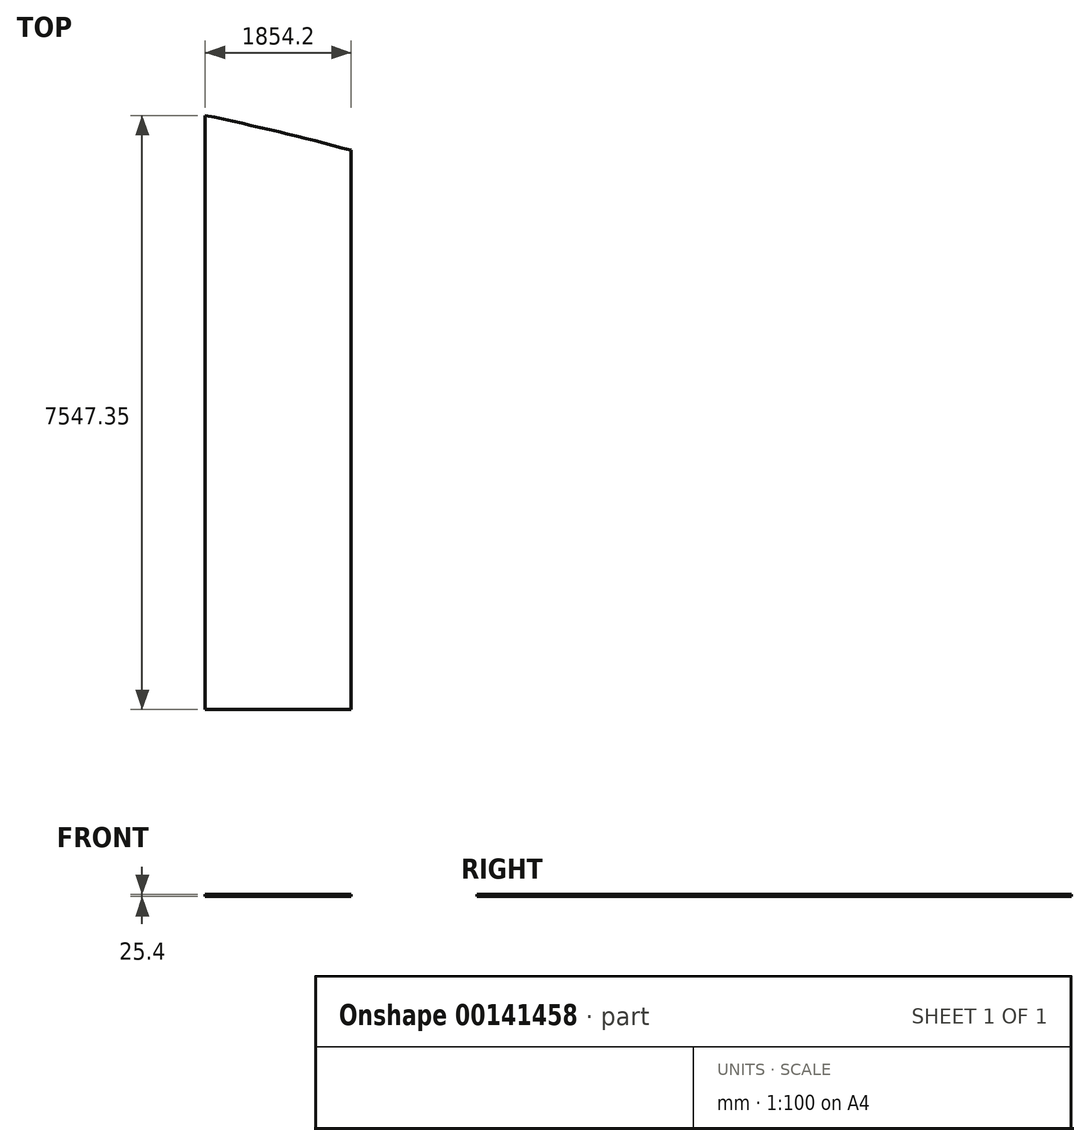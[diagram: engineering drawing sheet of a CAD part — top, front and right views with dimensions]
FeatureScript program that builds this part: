
annotation { "Feature Type Name" : "Feature", "Feature Type Description" : "" }
export const myFeature = defineFeature(function(context is Context, id is Id, definition is map)
    precondition{}
    {
        {
            var Q0;
            Q0=qCreatedBy(makeId("Top.planeOp"),FACE);
            var sketch = newSketch(context, id + "F0", { "sketchPlane" : qUnion([Q0])});
            skLineSegment(sketch, "E0", {"start": v(-1507.87, -4148.64) * mm, "end": v(346.33, -4148.64) * mm});
            skLineSegment(sketch, "E1", {"start": v(-1507.87, -4148.64) * mm, "end": v(-1507.87, 3398.71) * mm});
            skLineSegment(sketch, "E2", {"start": v(346.33, -4148.64) * mm, "end": v(346.33, 2955.23) * mm});
            skLineSegment(sketch, "E3", {"start": v(-580.77, -4148.64) * mm, "end": v(-580.77, 3190.69) * mm});
            skArc(sketch, "E4", {"start": v(346.33, 2955.23) * mm, "mid": v(-577.67, 3189.95) * mm, "end": v(-1507.87, 3398.71) * mm});
            skSolve(sketch);
        }
        {
            var Q0;
            {var subQ0=sQuery(id+"F0.wireOp",EDGE,"E1");Q0=makeQuery(id+"F0.imprint","IMPRINT",FACE,{"disambiguationData":[TD([[makeQuery(id+"F0.imprint","IMPRINT",EDGE,{"derivedFrom":subQ0}),-1.0]])]});}
            var Q1;
            {var subQ0=sQuery(id+"F0.wireOp",EDGE,"E2");Q1=makeQuery(id+"F0.imprint","IMPRINT",FACE,{"disambiguationData":[TD([[makeQuery(id+"F0.imprint","IMPRINT",EDGE,{"derivedFrom":subQ0}),1.0]])]});}
            extrude(context, id + "F1", {"entities" : qUnion([Q0, Q1]), "depth" : 25.4 * mm});
        }
    });
